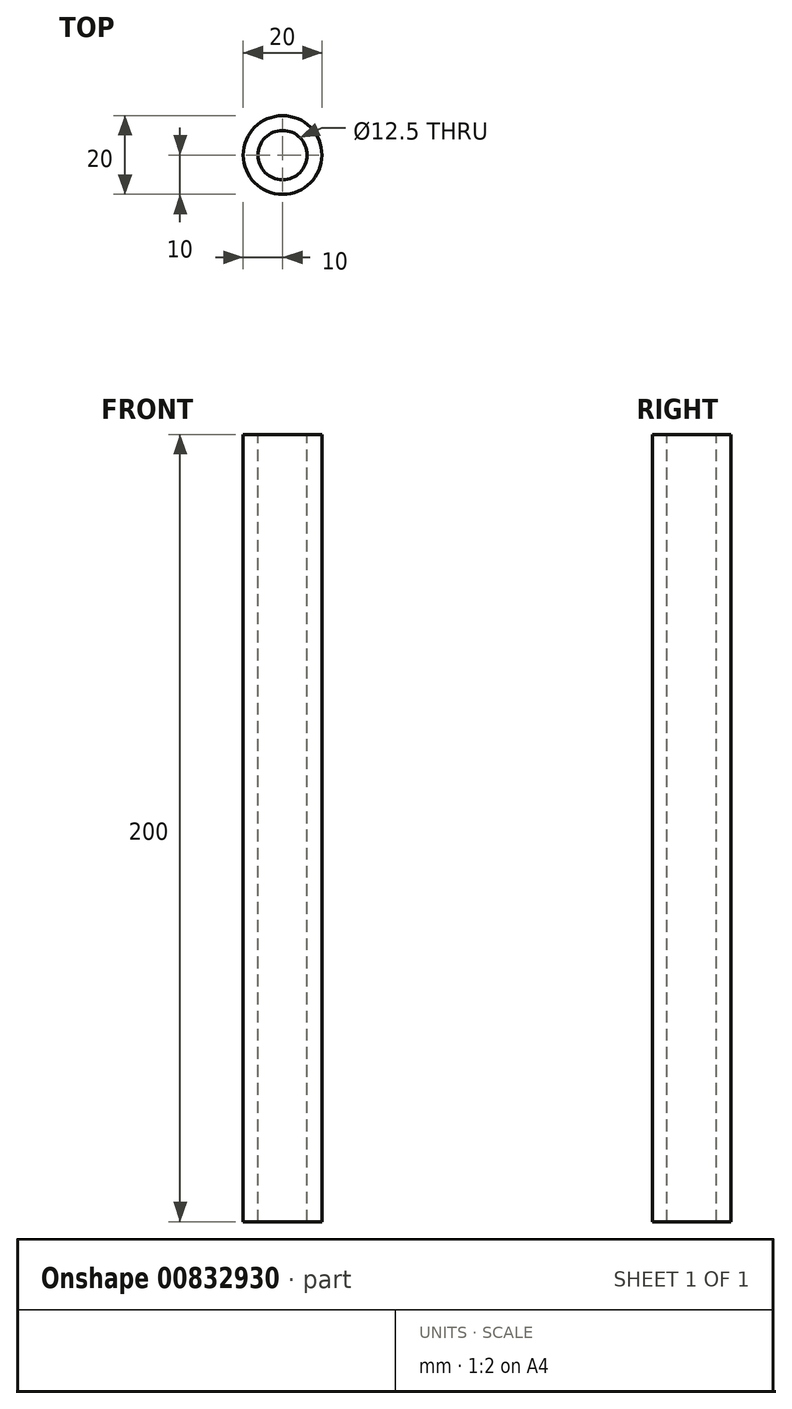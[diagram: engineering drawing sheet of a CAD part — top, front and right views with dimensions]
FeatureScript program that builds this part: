
annotation { "Feature Type Name" : "Feature", "Feature Type Description" : "" }
export const myFeature = defineFeature(function(context is Context, id is Id, definition is map)
    precondition{}
    {
        {
            var Q0;
            Q0=qCreatedBy(makeId("Top.planeOp"),FACE);
            var sketch = newSketch(context, id + "F0", { "sketchPlane" : qUnion([Q0])});
            skCircle(sketch, "E0", {"center": v(0, 0) * mm, "radius": 6.25 * mm});
            skCircle(sketch, "E1", {"center": v(0, 0) * mm, "radius": 10 * mm});
            skSolve(sketch);
        }
        {
            var Q0;
            Q0=makeQuery(id+"F0.imprint","IMPRINT",FACE,{"disambiguationData":[TD([[makeQuery(id+"F0.imprint","IMPRINT",EDGE,{"derivedFrom":sQuery(id+"F0.wireOp",EDGE,"E0")}),-1.0]])]});
            extrude(context, id + "F1", {"entities" : qUnion([Q0]), "oppositeDirection" : true, "depth" : 200 * mm, "offsetDistance" : 25 * mm});
        }
    });
